annotation { "Feature Type Name" : "Feature", "Feature Type Description" : "" }
export const myFeature = defineFeature(function(context is Context, id is Id, definition is map)
    precondition{}
    {
        {
            var Q0;
            Q0=qCreatedBy(makeId("Top.planeOp"),FACE);
            var sketch = newSketch(context, id + "F0", { "sketchPlane" : qUnion([Q0])});
            skLineSegment(sketch, "E0.bottom", {"start": v(-38.1, -19.05) * mm, "end": v(38.1, -19.05) * mm});
            skLineSegment(sketch, "E0.top", {"start": v(-38.1, 19.05) * mm, "end": v(38.1, 19.05) * mm});
            skLineSegment(sketch, "E0.left", {"start": v(-38.1, -19.05) * mm, "end": v(-38.1, 19.05) * mm});
            skLineSegment(sketch, "E0.right", {"start": v(38.1, -19.05) * mm, "end": v(38.1, 19.05) * mm});
            skPoint(sketch, "E0.middle", {"position": v(0, 0) * mm});
            skText(sketch, "E1", { "text": "EXPLORING TECH", "fontName": "OpenSans-Regular.ttf"});
            skPoint(sketch, "E2.33.internal.snap0", {"position": v(0, -8.02) * mm});
            skFitSpline(sketch, "E2", {"points": [v(4.72, -6.95) * mm, v(6.95, -7.86) * mm, v(9.6, -8.85) * mm, v(12.65, -10.17) * mm, v(15.46, -11.5) * mm, v(18.43, -12.32) * mm, v(22.4, -13.97) * mm, v(25.37, -15.37) * mm, v(27.52, -16.05) * mm, v(28.96, -14.63) * mm, v(28.96, -12.48) * mm, v(25.04, -11.08) * mm, v(20.09, -9.67) * mm, v(15.96, -8.02) * mm, v(11.74, -6.78) * mm, v(8.2, -5.54) * mm, v(5.47, -4.55) * mm, v(4.4, -3.4) * mm, v(4.64, -2.16) * mm, v(6.38, -1.42) * mm, v(8.03, 0) * mm, v(6.3, 0) * mm, v(2.9, -1.33) * mm, v(1.09, -3.9) * mm, v(0.84, -6.2) * mm, v(1.25, -6.7) * mm, v(1.34, -6.87) * mm, v(0, -8.02) * mm, v(0, -8.68) * mm, v(0, -9.26) * mm, v(0, -10.25) * mm, v(2.5, -10.34) * mm, v(2.99, -9.26) * mm, v(2.58, -8.02) * mm, v(3.07, -7.11) * mm, v(4.72, -6.95) * mm]});
            const initialGuessF0  = {"E1": [-0.03492, 0.00725, 1, 0, 0.0062]};
            skSetInitialGuess(sketch, initialGuessF0);
            skSolve(sketch);
        }
        {
            var Q0;
            Q0=makeQuery(id+"F0.imprint","IMPRINT",FACE,{"disambiguationData":[TD([[makeQuery(id+"F0.imprint","IMPRINT",EDGE,{"derivedFrom":sQuery(id+"F0.wireOp",EDGE,"E0.bottom")}),1.0]])]});
            extrude(context, id + "F1", {"entities" : qUnion([Q0]), "depth" : 6.35 * mm});
        }
    });